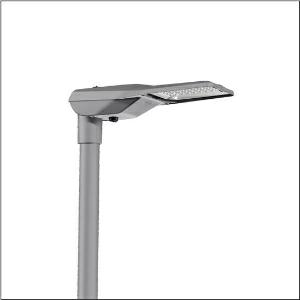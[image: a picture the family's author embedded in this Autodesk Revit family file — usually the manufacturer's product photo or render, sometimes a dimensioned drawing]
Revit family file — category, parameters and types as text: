
# Revit family: streetlight_sl_21_iq_mini___st1_0a_5xe2d61y08jb_b42a
name_source: partatom
category: Lighting Fixtures
units: mm (PartAtom-declared; Revit-internal decimal feet)

## family parameters
Cut with Voids When Loaded = No
Host = Face
Light Source = No
Part Type = Normal
Room Calculation Point = No
Round Connector Dimension = Use Diameter
Shared = No

## types (1)
- --- (1 x LED, 9730 lm, 72.5 W, 2700K)
    Apparent Load = 73 VA
    CIE Flux Codes = 40 73 97 100 100
    Color Rendering = 70
    Color Temperature = 2700K
    Default Elevation = 1800 mm
    Description = Streetlight SL 21 iQ mini, mast luminaire, primary light control with lens, of PMMA, primary optical cover: cover, of toughened safety glass, transparent, light distribution: ST1.0a, light emission: direct distribution, primary light characteristic: asymmetric, installation type: post-top, side-entry, LED, High Power LED, rated luminous flux: 9.730lm, luminous efficacy: 134lm/W, light colour: 727, colour temperature: 2700K, control: presetting dimming logarithmic, Street-Remote, Auto-Match, Temp-Guard, Lumen-Switch, Night-Set, Smart-Wire, Light-Fading, Desk-Remote (wireless, voltage-free reading and setting of iQ features in the workshop via application-optimized NFC function/RFID function), optimised constant luminous flux control (CLO 2.0), mains connection: 220..240V, AC, 50/60Hz, start of lifetime: 73W, end of service life: 76W, reduction: 33W, luminaire housing, of diecast aluminium, powder-coated, Siteco® metallic grey (DB 702S), corrosivity category C5 mid according to DIN EN ISO 12944, please order mast flange separately, inclination adjustable: 0°, 5°, 10°, 15°, sealing non-destructively replaceable, multi-level sealing system, length: 628mm, width: 235mm, height: 110mm, mast flange for spigot size: 42mm (side-entry): 5XC10008XM4, 60/48mm (side-entry/post-top): 5XC10108XM2, 76/60mm (side-entry/post-top): 5XC10108XM1, Smart Interface below and above, protection rating (complete): IP66, insulation class (complete): insulation class II (safety insulation), certification: CE, ENEC, ENEC+, VDE, impact resistance: IK09, permissible operating ambient temperature for outdoor applications: -40..+50°C, standard-compliant lighting for roads and squares, packaging unit: 1 piece

Light Distribution: ST1.0a
    Height = 110 mm
    Lamp = 1 x LED
    Lamp Light Flux = 9730 lm
    Lamp Power = 72.5 W
    Lamp count = 1
    Length = 625 mm
    Luminous efficacy = 134 lm/W
    Manufacturer = Siteco
    ModVariant = No
    Model = 5XE2D61Y08JB
    Number of Poles = 1
    OnlyDefault = Yes
    Power Factor = 1
    Product Name = Streetlight SL 21 iQ mini | ST1.0a
    Product group = mast luminaire | pylon top
    ProductGroupID = 6100
    Protection Class = Protection class II
    Protection Degree = IP 66
    RLX_Detail_Level = 1
    RLX_Emergency_Light_Flux = 0 lm
    RLX_Emergency_Type = 0
    RLX_Emergency_Type_DB = No
    RlxData = <blob elided: 92793 chars, md5=00915a8e>
    Socket = socket
    Standby Power = 0 W
    System Light Flux = 9730 lm
    System Power = 73 W
    Type Comments = factory setting: luminous flux: 100 % | dim-lin: 254 | 755 mA
    Type Image = l_1003514.jpg
    URL = http://relux.com
    VarID = @adj_044149
    Voltage = 0 V
    Weight = 0.00 kg
    Width = 234 mm

## geometry (parser evidence)
native form markers: Blend x4, Sweep x9
no freeform markers — native parametric forms only
